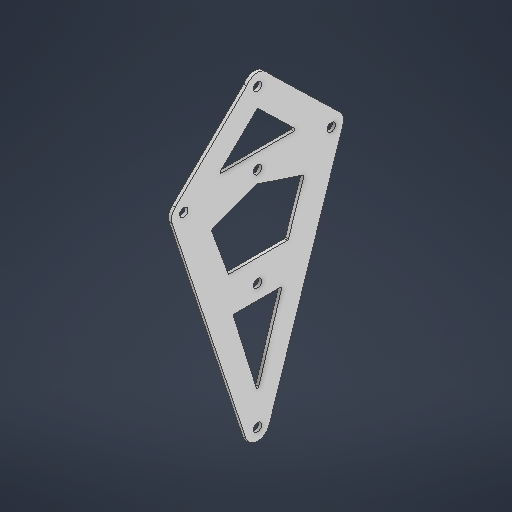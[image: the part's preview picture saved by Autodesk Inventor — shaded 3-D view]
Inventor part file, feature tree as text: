
AUTODESK INVENTOR PART (.ipt)
format: ipt  version: 2025.2 (Build 292293000, 293)  size: 250,368 bytes
history: native  units: in
note: dims shown in document units (in); Inventor stores cm internally (conversion verified against a paired STEP export)
features: extrude x1, sketch x1
ambient origin geometry x8: Origin, YZ Plane, XZ Plane, XY Plane, X Axis, Y Axis, Z Axis, Center Point
bodies: Solid1 (feature_tree)
feature tree (2):
  extrude  "Extrusion1"  Depth=0.025in
  sketch  "Sketch1"  dims[d0=0.5in d1=0.5in d2=0.5in d7=0.172in d8=0.172in d9=0.172in d10=0.172in d12=0.0625in d13=0.0in d16=0.172in d18=0.172in d19=1.0in d20=1.0in d21=0.8in d22=0.8in d23=0.5in d24=0.5in d25=0.025in d26=0.025in]
